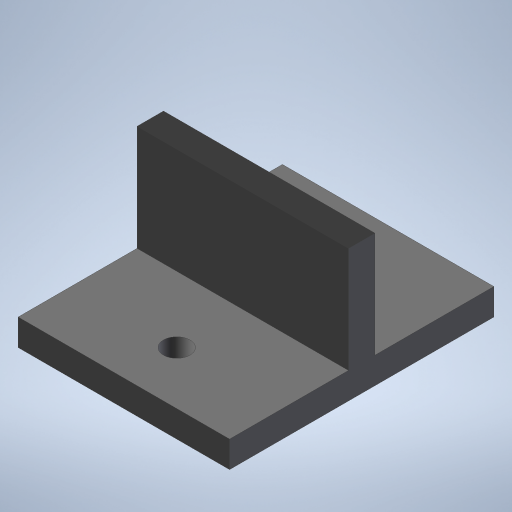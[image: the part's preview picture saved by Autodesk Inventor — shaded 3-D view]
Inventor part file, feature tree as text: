
AUTODESK INVENTOR PART (.ipt)
format: ipt  version: 2023 (Build 270158000, 158)  size: 227,840 bytes
history: native  units: mm
features: extrude x2, sketch x2
ambient origin geometry x8: Origin, YZ Plane, XZ Plane, XY Plane, X Axis, Y Axis, Z Axis, Center Point
bodies: Solid1 (feature_tree)
feature tree (4):
  extrude  "Extrusion1"  Depth=50.0mm
  extrude  "Extrusion2"  Depth=5.0mm
  sketch  "Sketch1"  dims[d0=40.0mm d1=50.0mm]
  sketch  "Sketch2"  dims[d2=5.0mm d3=5.0mm d4=10.0mm d5=10.0mm d6=20.0mm d7=5.0mm d8=0.0mm d9=5.0mm d10=22.5mm d11=20.0mm d12=0.0mm]
